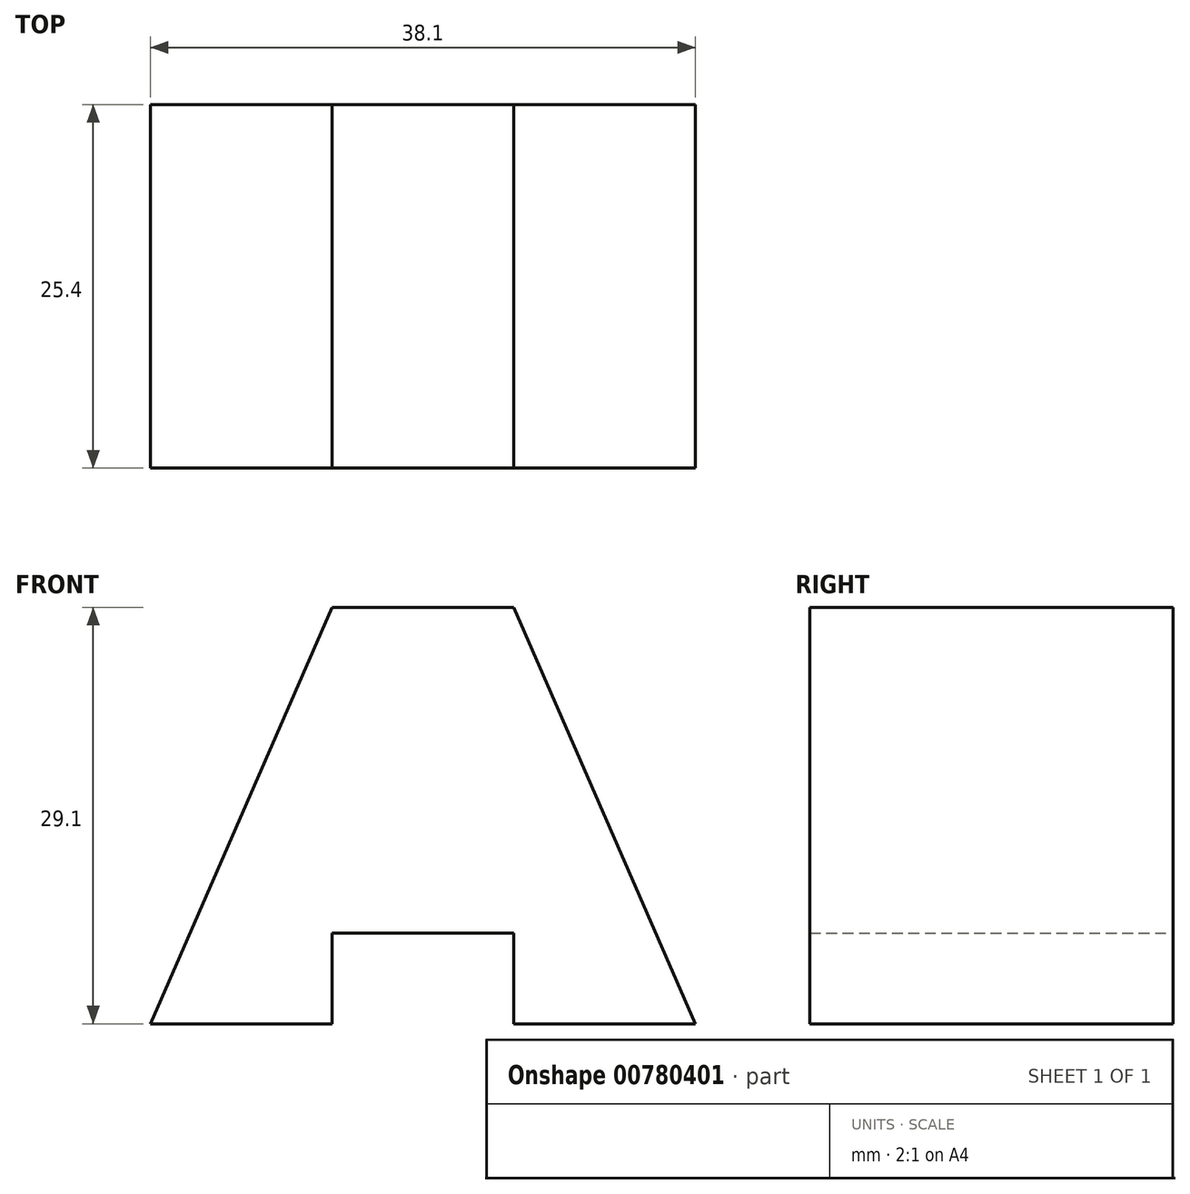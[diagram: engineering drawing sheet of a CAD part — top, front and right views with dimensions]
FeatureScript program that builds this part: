
annotation { "Feature Type Name" : "Feature", "Feature Type Description" : "" }
export const myFeature = defineFeature(function(context is Context, id is Id, definition is map)
    precondition{}
    {
        {
            var Q0;
            Q0=qCreatedBy(makeId("Front.planeOp"),FACE);
            var sketch = newSketch(context, id + "F0", { "sketchPlane" : qUnion([Q0])});
            skLineSegment(sketch, "E0", {"start": v(0, 0) * mm, "end": v(12.7, 0) * mm});
            skLineSegment(sketch, "E1", {"start": v(12.7, 0) * mm, "end": v(12.7, 6.35) * mm});
            skLineSegment(sketch, "E2", {"start": v(12.7, 6.35) * mm, "end": v(25.4, 6.35) * mm});
            skLineSegment(sketch, "E3", {"start": v(25.4, 6.35) * mm, "end": v(25.4, 0) * mm});
            skLineSegment(sketch, "E4", {"start": v(25.4, 0) * mm, "end": v(38.1, 0) * mm});
            skLineSegment(sketch, "E5", {"start": v(0, 0) * mm, "end": v(12.7, 29.1) * mm});
            skPoint(sketch, "E5.endSnap0", {"position": v(12.7, 3.17) * mm});
            skLineSegment(sketch, "E6", {"start": v(12.7, 29.1) * mm, "end": v(25.4, 29.1) * mm});
            skLineSegment(sketch, "E7", {"start": v(25.4, 29.1) * mm, "end": v(38.1, 0) * mm});
            skSolve(sketch);
        }
        {
            var Q0;
            Q0=makeQuery(id+"F0.imprint","IMPRINT",FACE,{"disambiguationData":[TD([[makeQuery(id+"F0.imprint","IMPRINT",EDGE,{"derivedFrom":sQuery(id+"F0.wireOp",EDGE,"E0")}),1.0]])]});
            extrude(context, id + "F1", {"entities" : qUnion([Q0]), "depth" : 25.4 * mm, "offsetDistance" : 25.4 * mm});
        }
    });
